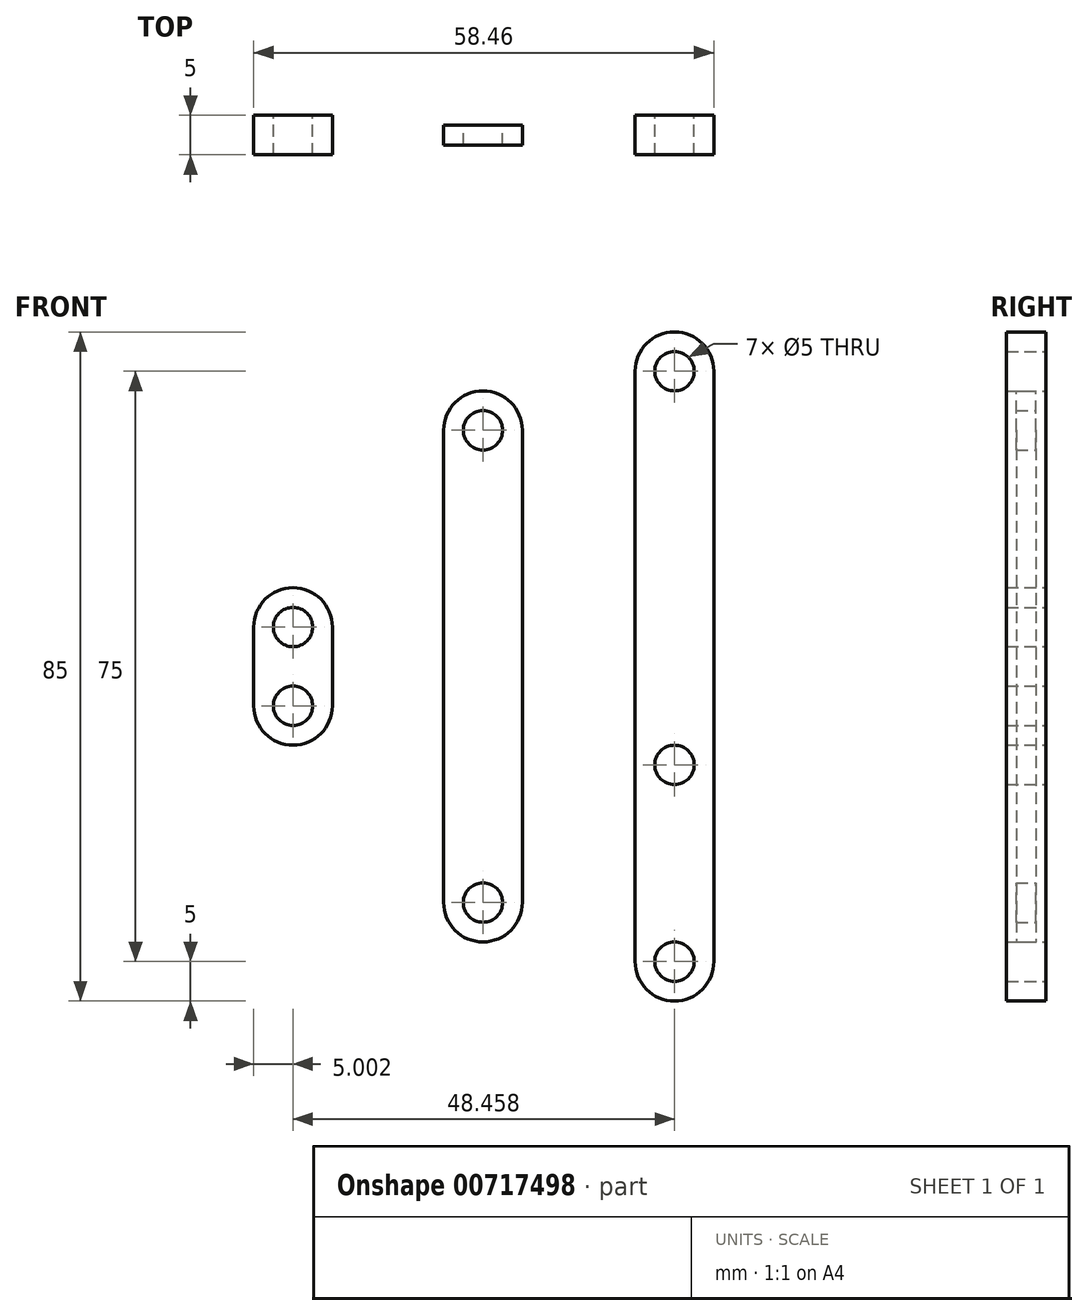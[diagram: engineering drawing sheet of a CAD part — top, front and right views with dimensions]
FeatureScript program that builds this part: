
annotation { "Feature Type Name" : "Feature", "Feature Type Description" : "" }
export const myFeature = defineFeature(function(context is Context, id is Id, definition is map)
    precondition{}
    {
        {
            var Q0;
            Q0=qCreatedBy(makeId("Front.planeOp"),FACE);
            var sketch = newSketch(context, id + "F0", { "sketchPlane" : qUnion([Q0])});
            skLineSegment(sketch, "E0", {"start": v(-5, 0) * mm, "end": v(5, 0) * mm, "construction": true});
            skArc(sketch, "E1", {"start": v(5, 37.5) * mm, "mid": v(0, 42.5) * mm, "end": v(-5, 37.5) * mm});
            skLineSegment(sketch, "E2", {"start": v(-5, 37.5) * mm, "end": v(-5, 0) * mm});
            skLineSegment(sketch, "E3", {"start": v(5, 37.5) * mm, "end": v(5, 0) * mm});
            skCircle(sketch, "E4", {"center": v(0, 37.5) * mm, "radius": 2.5 * mm});
            skLineSegment(sketch, "E5.MirrorCS", {"start": v(5, -37.5) * mm, "end": v(5, 0) * mm});
            skLineSegment(sketch, "E6.MirrorCS", {"start": v(-5, -37.5) * mm, "end": v(-5, 0) * mm});
            skCircle(sketch, "E7.MirrorC", {"center": v(0, -37.5) * mm, "radius": 2.5 * mm});
            skArc(sketch, "E8.MirrorCS", {"start": v(5, -37.5) * mm, "mid": v(0, -42.5) * mm, "end": v(-5, -37.5) * mm});
            skCircle(sketch, "E9", {"center": v(0, -12.5) * mm, "radius": 2.5 * mm});
            skPoint(sketch, "E9.centerSnap0", {"position": v(5, -18.75) * mm});
            skSolve(sketch);
        }
        {
            var Q0;
            Q0 = qSketchRegion(id + "FKXYk0SwZ8hMwPJ_0", true);
            var Q1;
            Q1=makeQuery(id+"F0.imprint","IMPRINT",FACE,{"disambiguationData":[TD([[makeQuery(id+"F0.imprint","IMPRINT",EDGE,{"derivedFrom":sQuery(id+"F0.wireOp",EDGE,"E1")}),1.0]])]});
            extrude(context, id + "F1", {"entities" : qUnion([Q0, Q1]), "depth" : 5 * mm, "offsetDistance" : 25 * mm, "symmetric" : true});
        }
        {
            var Q0;
            Q0=qCreatedBy(makeId("Front.planeOp"),FACE);
            var sketch = newSketch(context, id + "F2", { "sketchPlane" : qUnion([Q0])});
            skLineSegment(sketch, "E10", {"start": v(-29.33, 0) * mm, "end": v(-19.33, 0) * mm, "construction": true});
            skArc(sketch, "E11", {"start": v(-19.33, 30) * mm, "mid": v(-24.33, 35) * mm, "end": v(-29.33, 30) * mm});
            skLineSegment(sketch, "E12", {"start": v(-29.33, 30) * mm, "end": v(-29.33, 0) * mm});
            skLineSegment(sketch, "E13", {"start": v(-19.33, 30) * mm, "end": v(-19.33, 0) * mm});
            skCircle(sketch, "E14", {"center": v(-24.33, 30) * mm, "radius": 2.5 * mm});
            skLineSegment(sketch, "E15.MirrorCS", {"start": v(-19.33, -30) * mm, "end": v(-19.33, 0) * mm});
            skLineSegment(sketch, "E16.MirrorCS", {"start": v(-29.33, -30) * mm, "end": v(-29.33, 0) * mm});
            skCircle(sketch, "E17.MirrorC", {"center": v(-24.33, -30) * mm, "radius": 2.5 * mm});
            skArc(sketch, "E18.MirrorCS", {"start": v(-19.33, -30) * mm, "mid": v(-24.33, -35) * mm, "end": v(-29.33, -30) * mm});
            skSolve(sketch);
        }
        {
            var Q0;
            Q0 = qSketchRegion(id + "F2", true);
            extrude(context, id + "F3", {"entities" : qUnion([Q0]), "depth" : 2.5 * mm, "offsetDistance" : 25 * mm, "symmetric" : true});
        }
        {
            var Q0;
            Q0=qCreatedBy(makeId("Front.planeOp"),FACE);
            var sketch = newSketch(context, id + "F4", { "sketchPlane" : qUnion([Q0])});
            skLineSegment(sketch, "E19", {"start": v(-53.46, 0) * mm, "end": v(-43.46, 0) * mm, "construction": true});
            skArc(sketch, "E20", {"start": v(-43.46, 5) * mm, "mid": v(-48.46, 10) * mm, "end": v(-53.46, 5) * mm});
            skLineSegment(sketch, "E21", {"start": v(-53.46, 5) * mm, "end": v(-53.46, 0) * mm});
            skLineSegment(sketch, "E22", {"start": v(-43.46, 5) * mm, "end": v(-43.46, 0) * mm});
            skCircle(sketch, "E23", {"center": v(-48.46, 5) * mm, "radius": 2.5 * mm});
            skLineSegment(sketch, "E24.MirrorCS", {"start": v(-43.46, -5) * mm, "end": v(-43.46, 0) * mm});
            skLineSegment(sketch, "E25.MirrorCS", {"start": v(-53.46, -5) * mm, "end": v(-53.46, 0) * mm});
            skCircle(sketch, "E26.MirrorC", {"center": v(-48.46, -5) * mm, "radius": 2.5 * mm});
            skArc(sketch, "E27.MirrorCS", {"start": v(-43.46, -5) * mm, "mid": v(-48.46, -10) * mm, "end": v(-53.46, -5) * mm});
            skSolve(sketch);
        }
        {
            var Q0;
            Q0=makeQuery(id+"F4.imprint","IMPRINT",FACE,{"disambiguationData":[TD([[makeQuery(id+"F4.imprint","IMPRINT",EDGE,{"derivedFrom":sQuery(id+"F4.wireOp",EDGE,"E20")}),1.0]])]});
            extrude(context, id + "F5", {"entities" : qUnion([Q0]), "depth" : 5 * mm, "offsetDistance" : 25 * mm, "symmetric" : true});
        }
    });
